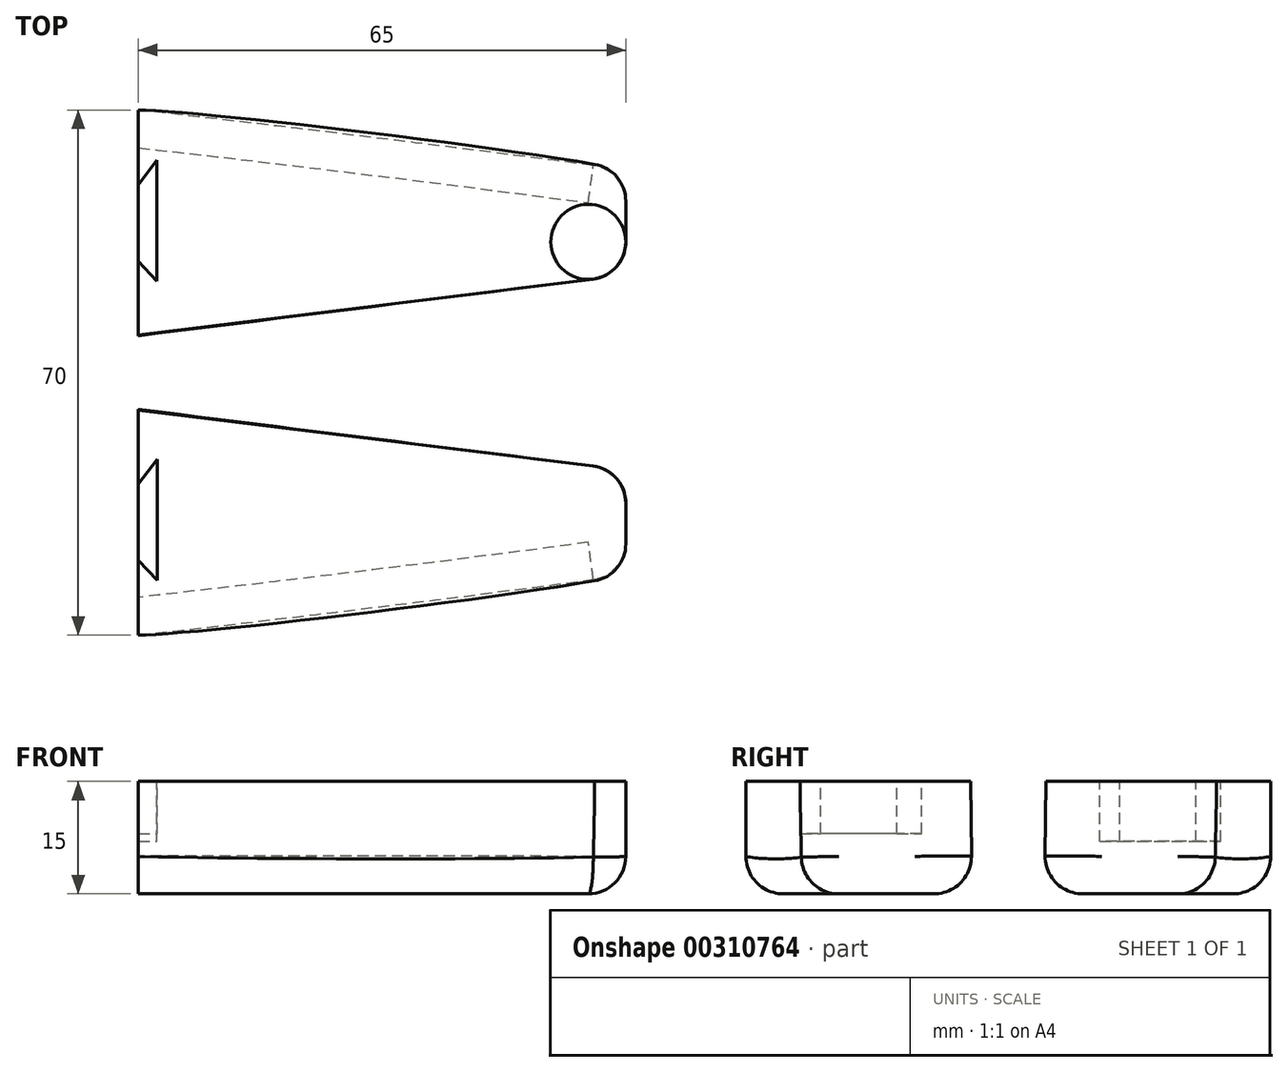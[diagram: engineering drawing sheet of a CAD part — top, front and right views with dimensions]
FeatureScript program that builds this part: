
annotation { "Feature Type Name" : "Feature", "Feature Type Description" : "" }
export const myFeature = defineFeature(function(context is Context, id is Id, definition is map)
    precondition{}
    {
        {
            var Q0;
            Q0=qCreatedBy(makeId("Right.planeOp"),FACE);
            var sketch = newSketch(context, id + "F0", { "sketchPlane" : qUnion([Q0])});
            skLineSegment(sketch, "E0", {"start": v(-5, 0) * mm, "end": v(-35, 0) * mm});
            skLineSegment(sketch, "E1", {"start": v(-35, 0) * mm, "end": v(-35, -15) * mm});
            skLineSegment(sketch, "E2", {"start": v(-35, -15) * mm, "end": v(-4.86, -15) * mm});
            skLineSegment(sketch, "E3", {"start": v(-4.86, -15) * mm, "end": v(-5, 0) * mm});
            skLineSegment(sketch, "E4.MirrorCS", {"start": v(5, 0) * mm, "end": v(35, 0) * mm});
            skLineSegment(sketch, "E5.MirrorCS", {"start": v(35, 0) * mm, "end": v(35, -15) * mm});
            skLineSegment(sketch, "E6.MirrorCS", {"start": v(35, -15) * mm, "end": v(4.86, -15) * mm});
            skLineSegment(sketch, "E7.MirrorCS", {"start": v(4.86, -15) * mm, "end": v(5, 0) * mm});
            skSolve(sketch);
        }
        {
            var Q0;
            Q0=qCreatedBy(makeId("Right.planeOp"),FACE);
            cPlane(context, id + "F1", {"entities" : qUnion([Q0]), "cplaneType" : CPlaneType.OFFSET, "offset" : 65 * mm, "width" : 150 * mm, "height" : 150 * mm});
        }
        {
            var Q0;
            Q0=qCreatedBy(id+"F1.planeOp",FACE);
            var sketch = newSketch(context, id + "F2", { "sketchPlane" : qUnion([Q0])});
            skLineSegment(sketch, "E8", {"start": v(-27, 0) * mm, "end": v(-13, 0) * mm});
            skLineSegment(sketch, "E9", {"start": v(-13, 0) * mm, "end": v(-13, -15) * mm});
            skLineSegment(sketch, "E10", {"start": v(-13, -15) * mm, "end": v(-27, -15) * mm});
            skLineSegment(sketch, "E11", {"start": v(-27, -15) * mm, "end": v(-27, 0) * mm});
            skLineSegment(sketch, "E12.MirrorCS", {"start": v(27, 0) * mm, "end": v(13, 0) * mm});
            skLineSegment(sketch, "E13.MirrorCS", {"start": v(27, -15) * mm, "end": v(27, 0) * mm});
            skLineSegment(sketch, "E14.MirrorCS", {"start": v(13, -15) * mm, "end": v(27, -15) * mm});
            skLineSegment(sketch, "E15.MirrorCS", {"start": v(13, 0) * mm, "end": v(13, -15) * mm});
            skSolve(sketch);
        }
        {
            var Q0;
            Q0=qCreatedBy(makeId("Top.planeOp"),FACE);
            var sketch = newSketch(context, id + "F3", { "sketchPlane" : qUnion([Q0])});
            skFitSpline(sketch, "E16", {"points": [v(0, 35) * mm, v(65, 27) * mm], "startDerivative": vector(21, 0) * mm, "endDerivative": vector(45, -9) * mm});
            skSolve(sketch);
        }
        {
            var Q0;
            Q0=qCreatedBy(makeId("Top.planeOp"),FACE);
            var sketch = newSketch(context, id + "F4", { "sketchPlane" : qUnion([Q0])});
            skFitSpline(sketch, "E17", {"points": [v(0, -35) * mm, v(65, -27) * mm], "startDerivative": vector(21, 0) * mm, "endDerivative": vector(45, 9) * mm});
            skSolve(sketch);
        }
        {
            var Q0;
            Q0=qCreatedBy(makeId("Top.planeOp"),FACE);
            var sketch = newSketch(context, id + "F5", { "sketchPlane" : qUnion([Q0])});
            skLineSegment(sketch, "E18", {"start": v(0, -4.86) * mm, "end": v(65, -13) * mm});
            skSolve(sketch);
        }
        {
            var Q0;
            Q0=qCreatedBy(makeId("Top.planeOp"),FACE);
            cPlane(context, id + "F6", {"entities" : qUnion([Q0]), "cplaneType" : CPlaneType.OFFSET, "offset" : 15 * mm, "oppositeDirection" : true, "width" : 150 * mm, "height" : 150 * mm});
        }
        {
            var Q0;
            Q0=qCreatedBy(id+"F6.planeOp",FACE);
            var sketch = newSketch(context, id + "F7", { "sketchPlane" : qUnion([Q0])});
            skLineSegment(sketch, "E19", {"start": v(65, -13) * mm, "end": v(0, -4.86) * mm});
            skSolve(sketch);
        }
        {
            var Q0;
            Q0=makeQuery(id+"F2.imprint","IMPRINT",FACE,{"disambiguationData":[TD([[makeQuery(id+"F2.imprint","IMPRINT",EDGE,{"derivedFrom":sQuery(id+"F2.wireOp",EDGE,"E12.MirrorCS")}),1.0]])]});
            var Q1;
            Q1=makeQuery(id+"F0.imprint","IMPRINT",FACE,{"disambiguationData":[TD([[makeQuery(id+"F0.imprint","IMPRINT",EDGE,{"derivedFrom":sQuery(id+"F0.wireOp",EDGE,"E4.MirrorCS")}),-1.0]])]});
            var Q2;
            Q2=sQuery(id+"F3.wireOp",EDGE,"E16");
            loft(context, id + "F8", {"addGuides" : true, "sheetProfilesArray" : [{ "sheetProfileEntities" : qUnion([Q0]) }, { "sheetProfileEntities" : qUnion([Q1]) }], "guidesArray" : [{ "guideEntities" : qUnion([Q2]), "guideDerivativeType" : LoftGuideDerivativeType.DEFAULT, "guideDerivativeMagnitude" : 1 }]});
        }
        {
            var Q0;
            Q0=makeQuery(id+"F0.imprint","IMPRINT",FACE,{"disambiguationData":[TD([[makeQuery(id+"F0.imprint","IMPRINT",EDGE,{"derivedFrom":sQuery(id+"F0.wireOp",EDGE,"E0")}),1.0]])]});
            var Q1;
            Q1=makeQuery(id+"F2.imprint","IMPRINT",FACE,{"disambiguationData":[TD([[makeQuery(id+"F2.imprint","IMPRINT",EDGE,{"derivedFrom":sQuery(id+"F2.wireOp",EDGE,"E8")}),-1.0]])]});
            var Q2;
            Q2=sQuery(id+"F4.wireOp",EDGE,"E17");
            loft(context, id + "F9", {"addGuides" : true, "sheetProfilesArray" : [{ "sheetProfileEntities" : qUnion([Q0]) }, { "sheetProfileEntities" : qUnion([Q1]) }], "guidesArray" : [{ "guideEntities" : qUnion([Q2]), "guideDerivativeType" : LoftGuideDerivativeType.DEFAULT, "guideDerivativeMagnitude" : 1 }]});
        }
        {
            var Q0;
            Q0=makeQuery(id+"F8.opLoft","MID_CAP_EDGE",EDGE,{"disambiguationData":[OSD([sQuery(id+"F2.wireOp",EDGE,"E13.MirrorCS"),sQuery(id+"F2.wireOp",EDGE,"E14.MirrorCS"),sQuery(id+"F2.wireOp",EDGE,"E15.MirrorCS")])],"capPos":0.0});
            var Q1;
            Q1=makeQuery(id+"F9.opLoft","MID_CAP_EDGE",EDGE,{"disambiguationData":[OSD([sQuery(id+"F2.wireOp",EDGE,"E9"),sQuery(id+"F2.wireOp",EDGE,"E10"),sQuery(id+"F2.wireOp",EDGE,"E11")])],"capPos":1.0});
            fillet(context, id + "F10", {"entities" : qUnion([Q0, Q1]), "radius" : 5 * mm, "tangentPropagation" : true, "allowEdgeOverflow" : false});
        }
        {
            var Q0;
            Q0=makeQuery(id+"F8.opLoft","SWEPT_EDGE",EDGE,{"disambiguationData":[OSD([sQuery(id+"F0.wireOp",EDGE,"E6.MirrorCS"),sQuery(id+"F0.wireOp",EDGE,"E7.MirrorCS"),sQuery(id+"F2.wireOp",EDGE,"E14.MirrorCS"),sQuery(id+"F2.wireOp",EDGE,"E15.MirrorCS")])]});
            var Q1;
            Q1=makeQuery(id+"F8.opLoft","SWEPT_EDGE",EDGE,{"disambiguationData":[OSD([sQuery(id+"F0.wireOp",EDGE,"E5.MirrorCS"),sQuery(id+"F0.wireOp",EDGE,"E6.MirrorCS"),sQuery(id+"F2.wireOp",EDGE,"E13.MirrorCS"),sQuery(id+"F2.wireOp",EDGE,"E14.MirrorCS")])]});
            var Q2;
            Q2=makeQuery(id+"F9.opLoft","SWEPT_EDGE",EDGE,{"disambiguationData":[OSD([sQuery(id+"F0.wireOp",EDGE,"E2"),sQuery(id+"F0.wireOp",EDGE,"E3"),sQuery(id+"F2.wireOp",EDGE,"E9"),sQuery(id+"F2.wireOp",EDGE,"E10")])]});
            var Q3;
            Q3=makeQuery(id+"F9.opLoft","SWEPT_EDGE",EDGE,{"disambiguationData":[OSD([sQuery(id+"F0.wireOp",EDGE,"E1"),sQuery(id+"F0.wireOp",EDGE,"E2"),sQuery(id+"F2.wireOp",EDGE,"E10"),sQuery(id+"F2.wireOp",EDGE,"E11")])]});
            fillet(context, id + "F11", {"entities" : qUnion([Q0, Q1, Q2, Q3]), "radius" : 5 * mm, "tangentPropagation" : true, "allowEdgeOverflow" : false});
        }
        {
            var Q0;
            Q0=makeQuery(id+"F8.opLoft","SWEPT_FACE",FACE,{"disambiguationData":[OSD([sQuery(id+"F0.wireOp",EDGE,"E4.MirrorCS"),sQuery(id+"F0.wireOp",EDGE,"E5.MirrorCS"),sQuery(id+"F0.wireOp",EDGE,"E7.MirrorCS"),sQuery(id+"F2.wireOp",EDGE,"E12.MirrorCS"),sQuery(id+"F2.wireOp",EDGE,"E15.MirrorCS"),sQuery(id+"F3.wireOp",EDGE,"E16")])]});
            var sketch = newSketch(context, id + "F12", { "sketchPlane" : qUnion([Q0])});
            skLineSegment(sketch, "E20", {"start": v(0, 25) * mm, "end": v(2.45, 28.34) * mm});
            skLineSegment(sketch, "E21", {"start": v(2.45, 28.34) * mm, "end": v(2.45, 12.2) * mm});
            skLineSegment(sketch, "E22", {"start": v(2.45, 12.2) * mm, "end": v(0, 14.86) * mm});
            skLineSegment(sketch, "E23", {"start": v(0, 14.86) * mm, "end": v(0, 25) * mm});
            skSolve(sketch);
        }
        {
            var Q0;
            Q0 = qSketchRegion(id + "F12", true);
            extrude(context, id + "F13", {"entities" : qUnion([Q0]), "operationType" : NewBodyOperationType.REMOVE, "oppositeDirection" : true, "depth" : 8 * mm});
        }
        {
            var Q0;
            Q0=makeQuery(id+"F9.opLoft","SWEPT_FACE",FACE,{"disambiguationData":[OSD([sQuery(id+"F0.wireOp",EDGE,"E0"),sQuery(id+"F0.wireOp",EDGE,"E3"),sQuery(id+"F2.wireOp",EDGE,"E8"),sQuery(id+"F2.wireOp",EDGE,"E9"),sQuery(id+"F2.wireOp",EDGE,"E11"),sQuery(id+"F4.wireOp",EDGE,"E17")])]});
            var sketch = newSketch(context, id + "F14", { "sketchPlane" : qUnion([Q0])});
            skLineSegment(sketch, "E24", {"start": v(0, -14.86) * mm, "end": v(2.54, -11.55) * mm});
            skLineSegment(sketch, "E25", {"start": v(2.54, -11.55) * mm, "end": v(2.54, -27.69) * mm});
            skLineSegment(sketch, "E26", {"start": v(2.54, -27.69) * mm, "end": v(0, -25) * mm});
            skLineSegment(sketch, "E27", {"start": v(0, -25) * mm, "end": v(0, -14.86) * mm});
            skSolve(sketch);
        }
        {
            var Q0;
            Q0 = qSketchRegion(id + "F14", true);
            extrude(context, id + "F15", {"entities" : qUnion([Q0]), "operationType" : NewBodyOperationType.REMOVE, "oppositeDirection" : true, "depth" : 7 * mm});
        }
    });
